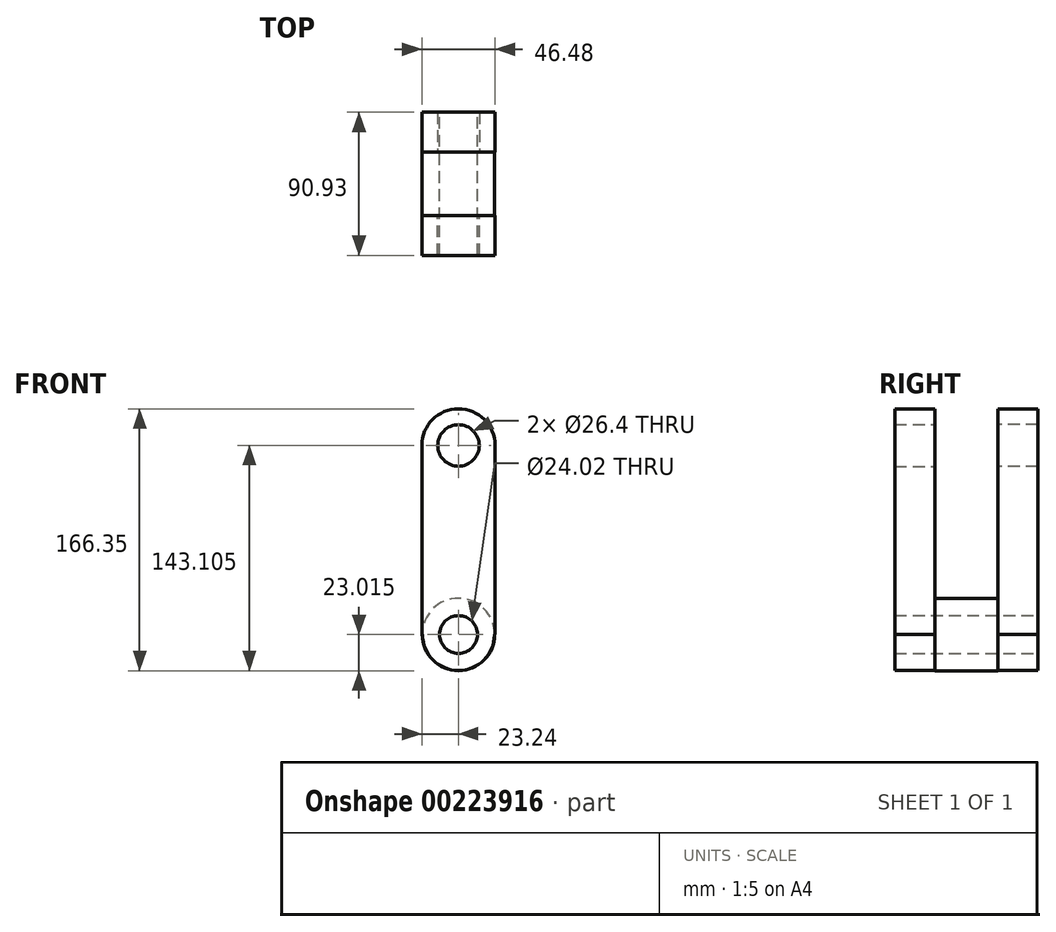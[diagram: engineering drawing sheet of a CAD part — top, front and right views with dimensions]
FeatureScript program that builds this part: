
annotation { "Feature Type Name" : "Feature", "Feature Type Description" : "" }
export const myFeature = defineFeature(function(context is Context, id is Id, definition is map)
    precondition{}
    {
        {
            var Q0;
            Q0=qCreatedBy(makeId("Front.planeOp"),FACE);
            var sketch = newSketch(context, id + "F0", { "sketchPlane" : qUnion([Q0])});
            skLineSegment(sketch, "E0.bottom", {"start": v(-23.24, 60.04) * mm, "end": v(23.24, 60.04) * mm});
            skLineSegment(sketch, "E0.top", {"start": v(-23.24, -60.04) * mm, "end": v(23.24, -60.04) * mm});
            skLineSegment(sketch, "E0.left", {"start": v(-23.24, 60.04) * mm, "end": v(-23.24, -60.04) * mm});
            skLineSegment(sketch, "E0.right", {"start": v(23.24, 60.04) * mm, "end": v(23.24, -60.04) * mm});
            skPoint(sketch, "E0.middle", {"position": v(0, 0) * mm});
            skCircle(sketch, "E1", {"center": v(0, -60.04) * mm, "radius": 22.8 * mm});
            skCircle(sketch, "E2", {"center": v(0, 60.04) * mm, "radius": 23.24 * mm});
            skCircle(sketch, "E3", {"center": v(0, -60.04) * mm, "radius": 12.01 * mm});
            skCircle(sketch, "E4", {"center": v(0, 60.04) * mm, "radius": 13.2 * mm});
            skSolve(sketch);
        }
        {
            var Q0;
            {var subQ1=sQuery(id+"F0.wireOp",EDGE,"E0.left");Q0=makeQuery(id+"F0.imprint","IMPRINT",FACE,{"disambiguationData":[TD([[makeQuery(id+"F0.imprint","IMPRINT",EDGE,{"derivedFrom":subQ1}),1.0]])]});}
            var Q1;
            {var subQ1=sQuery(id+"F0.wireOp",EDGE,"E0.bottom");var subQ3=sQuery(id+"F0.wireOp",EDGE,"E4");var subQ4=makeQuery(id+"F0.imprint","INTERSECT",VERTEX,{"disambiguationData":[OD(0.0)],"derivedFrom":[subQ1,subQ3]});Q1=makeQuery(id+"F0.imprint","IMPRINT",FACE,{"disambiguationData":[TD([[makeQuery(id+"F0.imprint","IMPRINT",EDGE,{"disambiguationData":[TD([[subQ4,-1.0]])],"derivedFrom":subQ3}),-1.0]])]});}
            var Q2;
            {var subQ0=sQuery(id+"F0.wireOp",EDGE,"E1");var subQ1=sQuery(id+"F0.wireOp",EDGE,"E0.top");var subQ2=makeQuery(id+"F0.imprint","INTERSECT",VERTEX,{"disambiguationData":[OD(0.0)],"derivedFrom":[subQ1,subQ0]});Q2=makeQuery(id+"F0.imprint","IMPRINT",FACE,{"disambiguationData":[TD([[makeQuery(id+"F0.imprint","IMPRINT",EDGE,{"disambiguationData":[TD([[subQ2,-1.0]])],"derivedFrom":subQ1}),1.0]])]});}
            var Q3;
            {var subQ0=sQuery(id+"F0.wireOp",EDGE,"E1");var subQ1=sQuery(id+"F0.wireOp",EDGE,"E0.top");var subQ2=makeQuery(id+"F0.imprint","INTERSECT",VERTEX,{"disambiguationData":[OD(0.0)],"derivedFrom":[subQ1,subQ0]});Q3=makeQuery(id+"F0.imprint","IMPRINT",FACE,{"disambiguationData":[TD([[makeQuery(id+"F0.imprint","IMPRINT",EDGE,{"disambiguationData":[TD([[subQ2,-1.0]])],"derivedFrom":subQ1}),-1.0]])]});}
            var Q4;
            {var subQ1=sQuery(id+"F0.wireOp",EDGE,"E0.bottom");var subQ3=sQuery(id+"F0.wireOp",EDGE,"E4");var subQ4=makeQuery(id+"F0.imprint","INTERSECT",VERTEX,{"disambiguationData":[OD(0.0)],"derivedFrom":[subQ1,subQ3]});Q4=makeQuery(id+"F0.imprint","IMPRINT",FACE,{"disambiguationData":[TD([[makeQuery(id+"F0.imprint","IMPRINT",EDGE,{"disambiguationData":[TD([[subQ4,1.0]])],"derivedFrom":subQ3}),-1.0]])]});}
            extrude(context, id + "F1", {"entities" : qUnion([Q0, Q1, Q2, Q3, Q4]), "depth" : 25.4 * mm});
        }
        {
            var Q0;
            Q0=makeQuery(id+"F1.opExtrude","CAP_FACE",FACE,{"disambiguationData":[OSD([sQuery(id+"F0.wireOp",EDGE,"E0.top"),sQuery(id+"F0.wireOp",EDGE,"E0.left"),sQuery(id+"F0.wireOp",EDGE,"E0.right"),sQuery(id+"F0.wireOp",EDGE,"E1"),sQuery(id+"F0.wireOp",EDGE,"E2"),sQuery(id+"F0.wireOp",EDGE,"E3"),sQuery(id+"F0.wireOp",EDGE,"E4")])],"isStart":true});
            var sketch = newSketch(context, id + "F2", { "sketchPlane" : qUnion([Q0])});
            skCircle(sketch, "E5", {"center": v(0, -60.04) * mm, "radius": 23.01 * mm});
            skSolve(sketch);
        }
        {
            var Q0;
            Q0 = qSketchRegion(id + "F2", true);
            extrude(context, id + "F3", {"entities" : qUnion([Q0]), "operationType" : NewBodyOperationType.ADD, "depth" : 20.07 * mm});
        }
        {
            var Q0;
            Q0=makeQuery(id+"F1.opExtrude","SWEPT_BODY",BODY,{"disambiguationData":[OSD([sQuery(id+"F0.wireOp",EDGE,"E0.top"),sQuery(id+"F0.wireOp",EDGE,"E0.left"),sQuery(id+"F0.wireOp",EDGE,"E0.right"),sQuery(id+"F0.wireOp",EDGE,"E1"),sQuery(id+"F0.wireOp",EDGE,"E2"),sQuery(id+"F0.wireOp",EDGE,"E3"),sQuery(id+"F0.wireOp",EDGE,"E4")])]});
            var Q1;
            Q1=makeQuery(id+"F3.opExtrude","CAP_FACE",FACE,{"disambiguationData":[OSD([sQuery(id+"F2.wireOp",EDGE,"E5")])],"isStart":false});
            mirror(context, id + "F4", {"operationType" : NewBodyOperationType.ADD, "entities" : qUnion([Q0]), "mirrorPlane" : qUnion([Q1])});
        }
        {
            var Q0;
            Q0=makeQuery(id+"F3.boolean.opBoolean","SPLIT",FACE,{"disambiguationData":[TD([makeQuery(id+"F1.opExtrude","SWEPT_FACE",FACE,{"disambiguationData":[OSD([sQuery(id+"F0.wireOp",EDGE,"E3")])]})])],"derivedFrom":makeQuery(id+"F3.opExtrude","CAP_FACE",FACE,{"disambiguationData":[OSD([sQuery(id+"F2.wireOp",EDGE,"E5")])],"isStart":true})});
            extrude(context, id + "F5", {"entities" : qUnion([Q0]), "operationType" : NewBodyOperationType.REMOVE, "endBound" : BoundingType.THROUGH_ALL, "oppositeDirection" : true, "depth" : 25.4 * mm});
        }
    });
